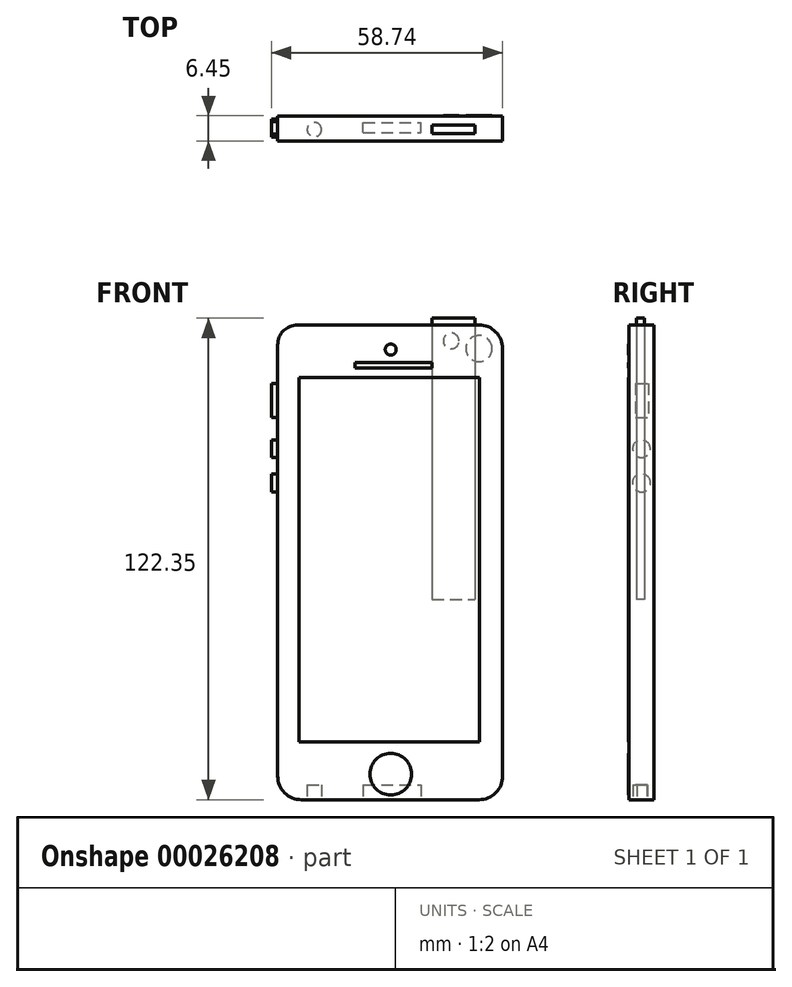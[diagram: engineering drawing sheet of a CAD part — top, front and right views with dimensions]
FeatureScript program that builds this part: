
annotation { "Feature Type Name" : "Feature", "Feature Type Description" : "" }
export const myFeature = defineFeature(function(context is Context, id is Id, definition is map)
    precondition{}
    {
        {
            var Q0;
            Q0=qCreatedBy(makeId("Front.planeOp"),FACE);
            var sketch = newSketch(context, id + "F0", { "sketchPlane" : qUnion([Q0])});
            skLineSegment(sketch, "E0.bottom", {"start": v(-28.71, 69.81) * mm, "end": v(28.44, 69.81) * mm});
            skLineSegment(sketch, "E0.top", {"start": v(-28.71, -50.84) * mm, "end": v(28.44, -50.84) * mm});
            skLineSegment(sketch, "E0.left", {"start": v(-28.71, 69.81) * mm, "end": v(-28.71, -50.84) * mm});
            skLineSegment(sketch, "E0.right", {"start": v(28.44, 69.81) * mm, "end": v(28.44, -50.84) * mm});
            skSolve(sketch);
        }
        {
            var Q0;
            Q0 = qSketchRegion(id + "F0", true);
            extrude(context, id + "F1", {"entities" : qUnion([Q0]), "depth" : 6.35 * mm});
        }
        {
            var Q0;
            Q0=makeQuery(id+"F1.opExtrude","SWEPT_EDGE",EDGE,{"disambiguationData":[OSD([sQuery(id+"F0.wireOp",EDGE,"E0.bottom"),sQuery(id+"F0.wireOp",EDGE,"E0.right")])]});
            fillet(context, id + "F2", {"entities" : qUnion([Q0]), "radius" : 6.02 * mm, "tangentPropagation" : true, "allowEdgeOverflow" : false});
        }
        {
            var Q0;
            Q0=makeQuery(id+"F1.opExtrude","SWEPT_EDGE",EDGE,{"disambiguationData":[OSD([sQuery(id+"F0.wireOp",EDGE,"E0.bottom"),sQuery(id+"F0.wireOp",EDGE,"E0.left")])]});
            fillet(context, id + "F3", {"entities" : qUnion([Q0]), "radius" : 5.08 * mm, "tangentPropagation" : true, "allowEdgeOverflow" : false});
        }
        {
            var Q0;
            Q0=makeQuery(id+"F1.opExtrude","SWEPT_EDGE",EDGE,{"disambiguationData":[OSD([sQuery(id+"F0.wireOp",EDGE,"E0.top"),sQuery(id+"F0.wireOp",EDGE,"E0.left")])]});
            fillet(context, id + "F4", {"entities" : qUnion([Q0]), "radius" : 6.02 * mm, "tangentPropagation" : true, "allowEdgeOverflow" : false});
        }
        {
            var Q0;
            Q0=makeQuery(id+"F1.opExtrude","SWEPT_EDGE",EDGE,{"disambiguationData":[OSD([sQuery(id+"F0.wireOp",EDGE,"E0.top"),sQuery(id+"F0.wireOp",EDGE,"E0.right")])]});
            fillet(context, id + "F5", {"entities" : qUnion([Q0]), "radius" : 6.02 * mm, "tangentPropagation" : true, "allowEdgeOverflow" : false});
        }
        {
            var Q0;
            Q0=makeQuery(id+"F1.opExtrude","SWEPT_FACE",FACE,{"disambiguationData":[OSD([sQuery(id+"F0.wireOp",EDGE,"E0.left")])]});
            var sketch = newSketch(context, id + "F6", { "sketchPlane" : qUnion([Q0])});
            skCircle(sketch, "E1", {"center": v(3.14, 38.34) * mm, "radius": 2.24 * mm});
            skCircle(sketch, "E2", {"center": v(3.14, 29.67) * mm, "radius": 2.29 * mm});
            skLineSegment(sketch, "E3.bottom", {"start": v(4.65, 54.96) * mm, "end": v(1.4, 54.96) * mm});
            skLineSegment(sketch, "E3.top", {"start": v(4.65, 46.31) * mm, "end": v(1.4, 46.31) * mm});
            skLineSegment(sketch, "E3.left", {"start": v(4.65, 54.96) * mm, "end": v(4.65, 46.31) * mm});
            skLineSegment(sketch, "E3.right", {"start": v(1.4, 54.96) * mm, "end": v(1.4, 46.31) * mm});
            skLineSegment(sketch, "E4.bottom", {"start": v(4.65, 54.96) * mm, "end": v(3.03, 54.96) * mm});
            skLineSegment(sketch, "E4.top", {"start": v(4.65, 46.31) * mm, "end": v(3.03, 46.31) * mm});
            skLineSegment(sketch, "E4.right", {"start": v(3.03, 54.96) * mm, "end": v(3.03, 46.31) * mm});
            skSolve(sketch);
        }
        {
            var Q0;
            Q0=makeQuery(id+"F6.imprint","IMPRINT",FACE,{"disambiguationData":[TD([[makeQuery(id+"F6.imprint","IMPRINT",EDGE,{"derivedFrom":sQuery(id+"F6.wireOp",EDGE,"E4.bottom")}),1.0]])]});
            var Q1;
            Q1=makeQuery(id+"F6.imprint","IMPRINT",FACE,{"disambiguationData":[TD([[makeQuery(id+"F6.imprint","IMPRINT",EDGE,{"derivedFrom":sQuery(id+"F6.wireOp",EDGE,"E3.bottom")}),1.0]])]});
            var Q2;
            Q2=makeQuery(id+"F6.imprint","IMPRINT",FACE,{"disambiguationData":[TD([[makeQuery(id+"F6.imprint","IMPRINT",EDGE,{"derivedFrom":sQuery(id+"F6.wireOp",EDGE,"E1")}),1.0]])]});
            var Q3;
            Q3=makeQuery(id+"F6.imprint","IMPRINT",FACE,{"disambiguationData":[TD([[makeQuery(id+"F6.imprint","IMPRINT",EDGE,{"derivedFrom":sQuery(id+"F6.wireOp",EDGE,"E2")}),1.0]])]});
            extrude(context, id + "F7", {"entities" : qUnion([Q0, Q1, Q2, Q3]), "depth" : 1.59 * mm});
        }
        {
            var Q0;
            Q0=makeQuery(id+"F1.opExtrude","CAP_FACE",FACE,{"disambiguationData":[OSD([sQuery(id+"F0.wireOp",EDGE,"E0.bottom"),sQuery(id+"F0.wireOp",EDGE,"E0.top"),sQuery(id+"F0.wireOp",EDGE,"E0.left"),sQuery(id+"F0.wireOp",EDGE,"E0.right")])],"isStart":true});
            var sketch = newSketch(context, id + "F8", { "sketchPlane" : qUnion([Q0])});
            skCircle(sketch, "E5", {"center": v(-22.42, 63.8) * mm, "radius": 3.32 * mm});
            skCircle(sketch, "E6", {"center": v(-15.37, 65.74) * mm, "radius": 2 * mm});
            skSolve(sketch);
        }
        {
            var Q0;
            Q0=qCreatedBy(makeId("Top.planeOp"),FACE);
            var sketch = newSketch(context, id + "F9", { "sketchPlane" : qUnion([Q0])});
            skLineSegment(sketch, "E7.bottom", {"start": v(10.47, -2.36) * mm, "end": v(21.37, -2.36) * mm});
            skLineSegment(sketch, "E7.top", {"start": v(10.47, -4.43) * mm, "end": v(21.37, -4.43) * mm});
            skLineSegment(sketch, "E7.left", {"start": v(10.47, -2.36) * mm, "end": v(10.47, -4.43) * mm});
            skLineSegment(sketch, "E7.right", {"start": v(21.37, -2.36) * mm, "end": v(21.37, -4.43) * mm});
            skSolve(sketch);
        }
        {
            var Q0;
            Q0 = qSketchRegion(id + "F9", true);
            extrude(context, id + "F10", {"entities" : qUnion([Q0]), "depth" : 71.51 * mm});
        }
        {
            var Q0;
            Q0=makeQuery(id+"F1.opExtrude","CAP_FACE",FACE,{"disambiguationData":[OSD([sQuery(id+"F0.wireOp",EDGE,"E0.bottom"),sQuery(id+"F0.wireOp",EDGE,"E0.top"),sQuery(id+"F0.wireOp",EDGE,"E0.left"),sQuery(id+"F0.wireOp",EDGE,"E0.right")])],"isStart":false});
            var sketch = newSketch(context, id + "F11", { "sketchPlane" : qUnion([Q0])});
            skLineSegment(sketch, "E8.bottom", {"start": v(-23.33, 56.4) * mm, "end": v(22.5, 56.4) * mm});
            skLineSegment(sketch, "E8.top", {"start": v(-23.33, -36.1) * mm, "end": v(22.5, -36.1) * mm});
            skLineSegment(sketch, "E8.left", {"start": v(-23.33, 56.4) * mm, "end": v(-23.33, -36.1) * mm});
            skLineSegment(sketch, "E8.right", {"start": v(22.5, 56.4) * mm, "end": v(22.5, -36.1) * mm});
            skCircle(sketch, "E9", {"center": v(0, -44.33) * mm, "radius": 5.3 * mm});
            skLineSegment(sketch, "E10.bottom", {"start": v(-9.06, 60.25) * mm, "end": v(10.43, 60.25) * mm});
            skLineSegment(sketch, "E10.top", {"start": v(-9.06, 58.88) * mm, "end": v(10.43, 58.88) * mm});
            skLineSegment(sketch, "E10.left", {"start": v(-9.06, 60.25) * mm, "end": v(-9.06, 58.88) * mm});
            skLineSegment(sketch, "E10.right", {"start": v(10.43, 60.25) * mm, "end": v(10.43, 58.88) * mm});
            skCircle(sketch, "E11", {"center": v(0, 63.54) * mm, "radius": 1.4 * mm});
            skSolve(sketch);
        }
        {
            var Q0;
            Q0 = qSketchRegion(id + "F11", true);
            extrude(context, id + "F12", {"entities" : qUnion([Q0]), "depth" : 0.05 * mm});
        }
        {
            var Q0;
            Q0 = qSketchRegion(id + "F8", true);
            extrude(context, id + "F13", {"entities" : qUnion([Q0]), "depth" : 0.05 * mm});
        }
        {
            var Q0;
            Q0=makeQuery(id+"F1.opExtrude","SWEPT_FACE",FACE,{"disambiguationData":[OSD([sQuery(id+"F0.wireOp",EDGE,"E0.top")])]});
            var sketch = newSketch(context, id + "F14", { "sketchPlane" : qUnion([Q0])});
            skCircle(sketch, "E12", {"center": v(-19.39, 3.49) * mm, "radius": 1.83 * mm});
            skLineSegment(sketch, "E13.bottom", {"start": v(-6.98, 4.28) * mm, "end": v(7.69, 4.28) * mm});
            skLineSegment(sketch, "E13.top", {"start": v(-6.98, 1.71) * mm, "end": v(7.69, 1.71) * mm});
            skLineSegment(sketch, "E13.left", {"start": v(-6.98, 4.28) * mm, "end": v(-6.98, 1.71) * mm});
            skLineSegment(sketch, "E13.right", {"start": v(7.69, 4.28) * mm, "end": v(7.69, 1.71) * mm});
            skSolve(sketch);
        }
        {
            var Q0;
            Q0 = qSketchRegion(id + "F14", true);
            extrude(context, id + "F15", {"entities" : qUnion([Q0]), "oppositeDirection" : true, "depth" : 3.82 * mm});
        }
    });
